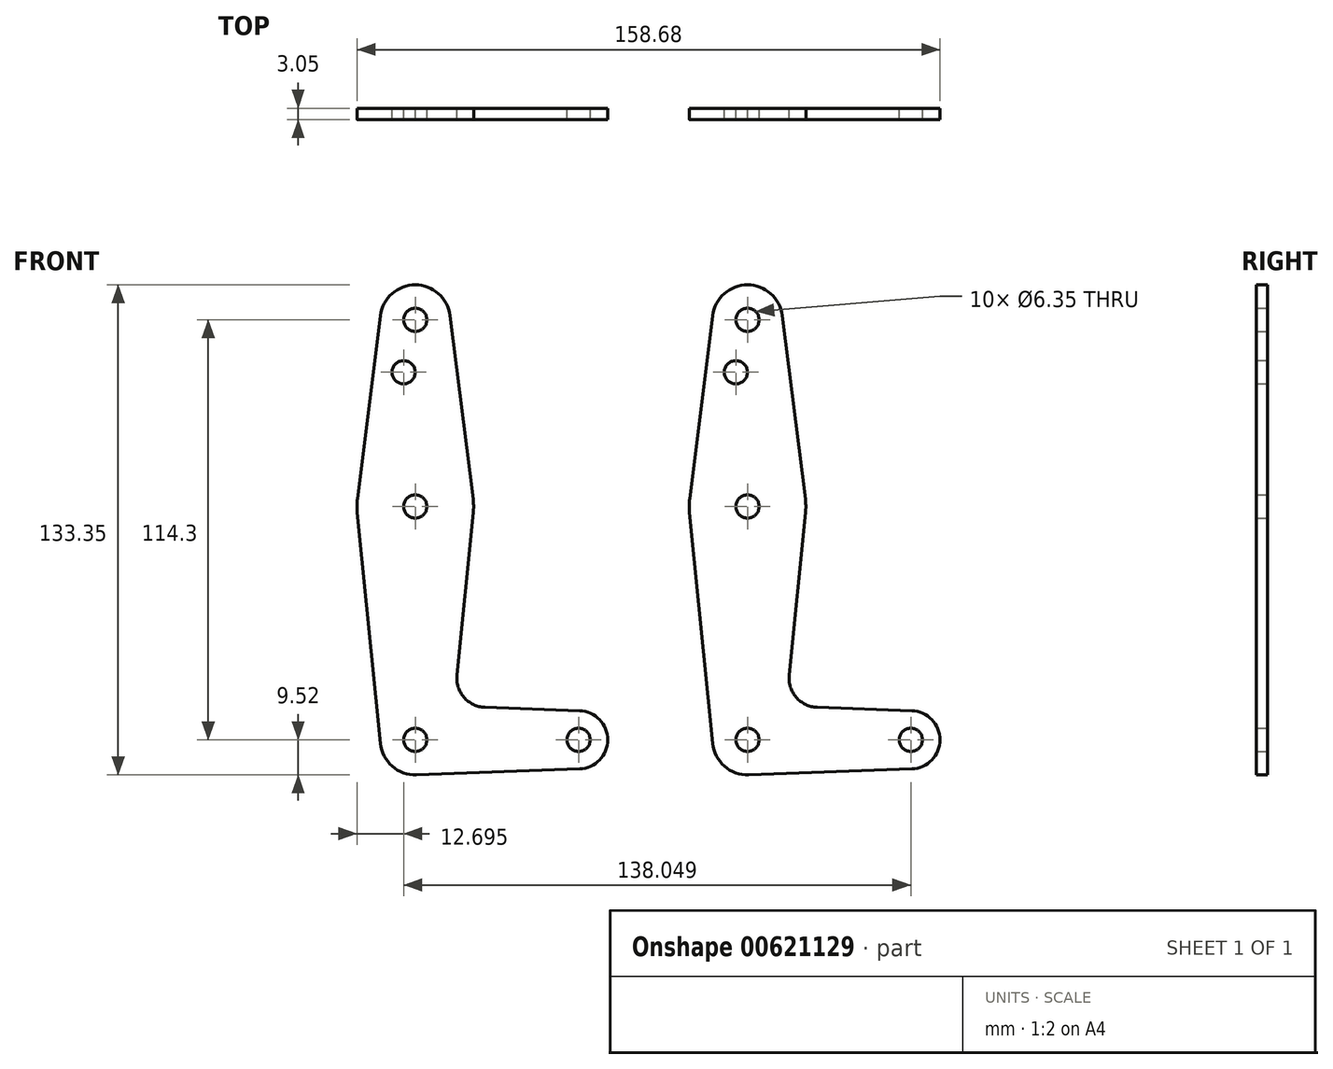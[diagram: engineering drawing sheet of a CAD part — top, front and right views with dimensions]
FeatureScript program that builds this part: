
annotation { "Feature Type Name" : "Feature", "Feature Type Description" : "" }
export const myFeature = defineFeature(function(context is Context, id is Id, definition is map)
    precondition{}
    {
        {
            var Q0;
            Q0=qCreatedBy(makeId("Front.planeOp"),FACE);
            var sketch = newSketch(context, id + "F0", { "sketchPlane" : qUnion([Q0])});
            skLineSegment(sketch, "E0", {"start": v(0, 0) * mm, "end": v(0, 114.3) * mm, "construction": true});
            skLineSegment(sketch, "E1", {"start": v(0, 0) * mm, "end": v(44.45, 0) * mm, "construction": true});
            skCircle(sketch, "E2", {"center": v(0, 0) * mm, "radius": 9.53 * mm});
            skCircle(sketch, "E3", {"center": v(44.45, 0) * mm, "radius": 7.94 * mm});
            skCircle(sketch, "E4", {"center": v(0, 114.3) * mm, "radius": 9.53 * mm});
            skCircle(sketch, "E5", {"center": v(0, 63.5) * mm, "radius": 15.88 * mm});
            skLineSegment(sketch, "E6", {"start": v(-9.45, 115.5) * mm, "end": v(-15.75, 65.48) * mm});
            skLineSegment(sketch, "E7", {"start": v(-9.48, -0.95) * mm, "end": v(-15.8, 61.91) * mm});
            skLineSegment(sketch, "E8", {"start": v(0.34, -9.52) * mm, "end": v(44.73, -7.93) * mm});
            skLineSegment(sketch, "E9.MirrorCS", {"start": v(9.45, 115.5) * mm, "end": v(15.75, 65.48) * mm});
            skLineSegment(sketch, "E10.MirrorCS", {"start": v(11.34, 17.6) * mm, "end": v(15.8, 61.91) * mm});
            skLineSegment(sketch, "E11.MirrorCS", {"start": v(18.97, 8.85) * mm, "end": v(44.73, 7.93) * mm});
            skCircle(sketch, "E12", {"center": v(0, 114.3) * mm, "radius": 3.18 * mm});
            skCircle(sketch, "E13", {"center": v(0, 63.5) * mm, "radius": 3.18 * mm});
            skCircle(sketch, "E14", {"center": v(-3.18, 100.03) * mm, "radius": 3.18 * mm});
            skCircle(sketch, "E15", {"center": v(0, 0) * mm, "radius": 3.18 * mm});
            skCircle(sketch, "E16", {"center": v(44.45, 0) * mm, "radius": 3.18 * mm});
            skPoint(sketch, "E17.newPointA", {"position": v(9.48, -0.95) * mm});
            skPoint(sketch, "E17.newPointB", {"position": v(0.34, 9.52) * mm});
            skArc(sketch, "E17.filletArc", {"start": v(11.34, 17.6) * mm, "mid": v(13.26, 11.57) * mm, "end": v(18.97, 8.85) * mm});
            skSolve(sketch);
        }
        {
            var Q0;
            Q0=makeQuery(id+"F0.imprint","IMPRINT",FACE,{"disambiguationData":[TD([[makeQuery(id+"F0.imprint","IMPRINT",EDGE,{"derivedFrom":sQuery(id+"F0.wireOp",EDGE,"E12")}),-1.0]])]});
            var Q1;
            {var subQ1=sQuery(id+"F0.wireOp",EDGE,"E6");Q1=makeQuery(id+"F0.imprint","IMPRINT",FACE,{"disambiguationData":[TD([[makeQuery(id+"F0.imprint","IMPRINT",EDGE,{"derivedFrom":subQ1}),1.0]])]});}
            var Q2;
            Q2=makeQuery(id+"F0.imprint","IMPRINT",FACE,{"disambiguationData":[TD([[makeQuery(id+"F0.imprint","IMPRINT",EDGE,{"derivedFrom":sQuery(id+"F0.wireOp",EDGE,"E13")}),-1.0]])]});
            var Q3;
            {var subQ0=sQuery(id+"F0.wireOp",EDGE,"E7");Q3=makeQuery(id+"F0.imprint","IMPRINT",FACE,{"disambiguationData":[TD([[makeQuery(id+"F0.imprint","IMPRINT",EDGE,{"derivedFrom":subQ0}),-1.0]])]});}
            var Q4;
            Q4=makeQuery(id+"F0.imprint","IMPRINT",FACE,{"disambiguationData":[TD([[makeQuery(id+"F0.imprint","IMPRINT",EDGE,{"derivedFrom":sQuery(id+"F0.wireOp",EDGE,"E15")}),-1.0]])]});
            var Q5;
            Q5=makeQuery(id+"F0.imprint","IMPRINT",FACE,{"disambiguationData":[TD([[makeQuery(id+"F0.imprint","IMPRINT",EDGE,{"derivedFrom":sQuery(id+"F0.wireOp",EDGE,"E16")}),-1.0]])]});
            extrude(context, id + "F1", {"entities" : qUnion([Q0, Q1, Q2, Q3, Q4, Q5]), "depth" : 3.05 * mm, "offsetDistance" : 25.4 * mm});
        }
        {
            var Q0;
            Q0=makeQuery(id+"F1.opExtrude","SWEPT_BODY",BODY,{"disambiguationData":[OSD([sQuery(id+"F0.wireOp",EDGE,"E2"),sQuery(id+"F0.wireOp",EDGE,"E3"),sQuery(id+"F0.wireOp",EDGE,"E4"),sQuery(id+"F0.wireOp",EDGE,"E5"),sQuery(id+"F0.wireOp",EDGE,"E6"),sQuery(id+"F0.wireOp",EDGE,"E7"),sQuery(id+"F0.wireOp",EDGE,"E8"),sQuery(id+"F0.wireOp",EDGE,"E9.MirrorCS"),sQuery(id+"F0.wireOp",EDGE,"E10.MirrorCS"),sQuery(id+"F0.wireOp",EDGE,"E11.MirrorCS"),sQuery(id+"F0.wireOp",EDGE,"E12"),sQuery(id+"F0.wireOp",EDGE,"E13"),sQuery(id+"F0.wireOp",EDGE,"E14"),sQuery(id+"F0.wireOp",EDGE,"E15"),sQuery(id+"F0.wireOp",EDGE,"E16"),sQuery(id+"F0.wireOp",EDGE,"E17.filletArc")])]});
            transform(context, id + "F2", {"entities" : qUnion([Q0]), "transformType" : TransformType.TRANSLATION_3D, "dx" : 90.42 * mm, "dy" : 0 * mm, "dz" : 0 * mm, "makeCopy" : true});
        }
    });
